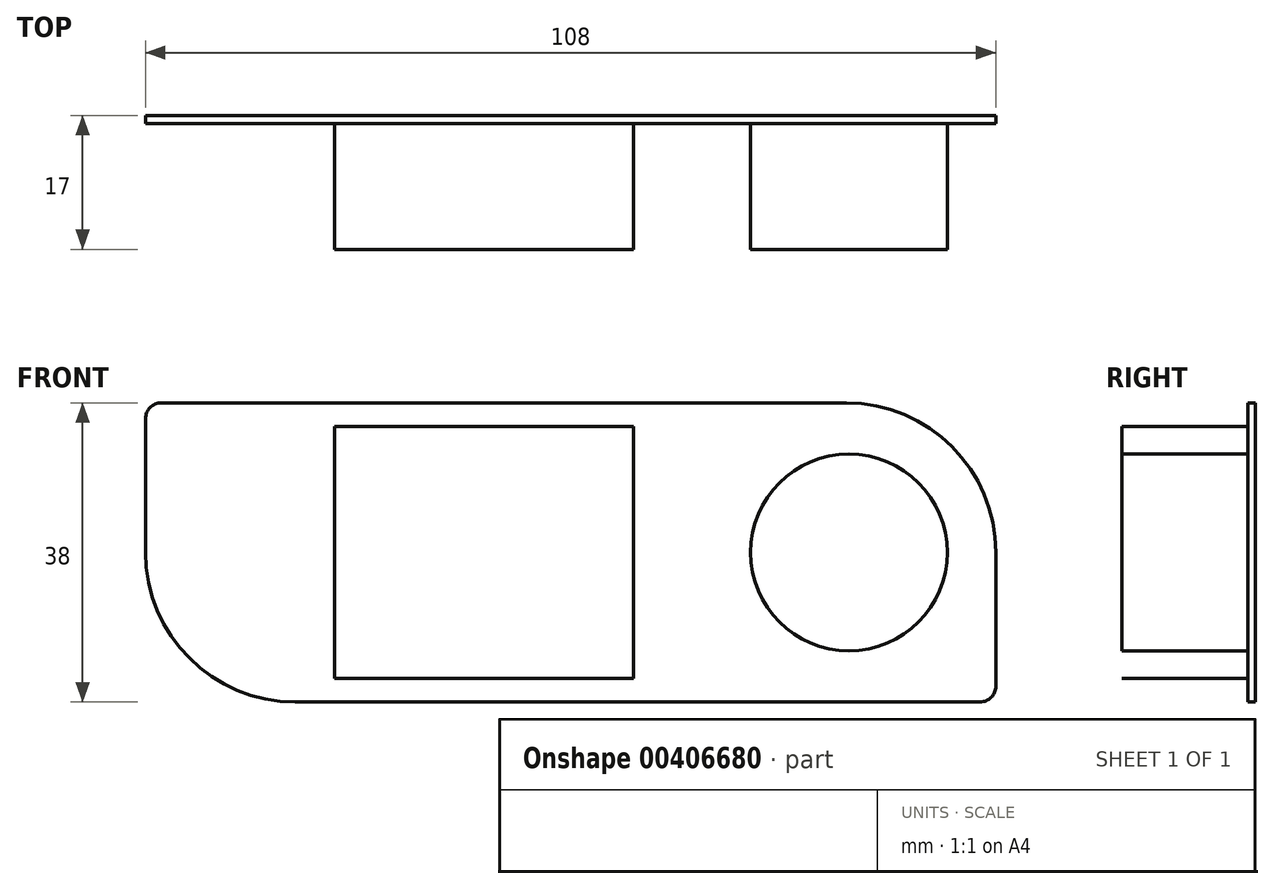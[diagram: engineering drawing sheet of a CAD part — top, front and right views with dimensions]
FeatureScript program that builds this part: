
annotation { "Feature Type Name" : "Feature", "Feature Type Description" : "" }
export const myFeature = defineFeature(function(context is Context, id is Id, definition is map)
    precondition{}
    {
        {
            var Q0;
            Q0=qCreatedBy(makeId("Front.planeOp"),FACE);
            var sketch = newSketch(context, id + "F0", { "sketchPlane" : qUnion([Q0])});
            skLineSegment(sketch, "E0.bottom", {"start": v(35, 19) * mm, "end": v(-52, 19) * mm});
            skLineSegment(sketch, "E0.top", {"start": v(52, -19) * mm, "end": v(-35, -19) * mm});
            skLineSegment(sketch, "E0.left", {"start": v(54, 0) * mm, "end": v(54, -17) * mm});
            skLineSegment(sketch, "E0.right", {"start": v(-54, 17) * mm, "end": v(-54, 0) * mm});
            skPoint(sketch, "E0.middle", {"position": v(0, 0) * mm});
            skPoint(sketch, "E1.visualSharp", {"position": v(-54, 19) * mm});
            skArc(sketch, "E1.filletArc", {"start": v(-52, 19) * mm, "mid": v(-53.41, 18.41) * mm, "end": v(-54, 17) * mm});
            skPoint(sketch, "E2.visualSharp", {"position": v(-54, -19) * mm});
            skArc(sketch, "E2.filletArc", {"start": v(-54, 0) * mm, "mid": v(-48.44, -13.44) * mm, "end": v(-35, -19) * mm});
            skPoint(sketch, "E3.visualSharp", {"position": v(54, 19) * mm});
            skArc(sketch, "E3.filletArc", {"start": v(54, 0) * mm, "mid": v(48.44, 13.44) * mm, "end": v(35, 19) * mm});
            skPoint(sketch, "E4.visualSharp", {"position": v(54, -19) * mm});
            skArc(sketch, "E4.filletArc", {"start": v(52, -19) * mm, "mid": v(53.41, -18.41) * mm, "end": v(54, -17) * mm});
            skSolve(sketch);
        }
        {
            var Q0;
            Q0=makeQuery(id+"F0.imprint","IMPRINT",FACE,{"disambiguationData":[TD([[makeQuery(id+"F0.imprint","IMPRINT",EDGE,{"derivedFrom":sQuery(id+"F0.wireOp",EDGE,"E0.bottom")}),1.0]])]});
            extrude(context, id + "F1", {"entities" : qUnion([Q0]), "depth" : 1 * mm});
        }
        {
            var Q0;
            Q0=makeQuery(id+"F1.opExtrude","CAP_FACE",FACE,{"disambiguationData":[OSD([sQuery(id+"F0.wireOp",EDGE,"E0.bottom"),sQuery(id+"F0.wireOp",EDGE,"E0.top"),sQuery(id+"F0.wireOp",EDGE,"E0.left"),sQuery(id+"F0.wireOp",EDGE,"E0.right"),sQuery(id+"F0.wireOp",EDGE,"E1.filletArc"),sQuery(id+"F0.wireOp",EDGE,"E2.filletArc"),sQuery(id+"F0.wireOp",EDGE,"E3.filletArc"),sQuery(id+"F0.wireOp",EDGE,"E4.filletArc")])],"isStart":false});
            var sketch = newSketch(context, id + "F2", { "sketchPlane" : qUnion([Q0])});
            skLineSegment(sketch, "E5.bottom", {"start": v(-30, 16) * mm, "end": v(8, 16) * mm});
            skLineSegment(sketch, "E5.top", {"start": v(-30, -16) * mm, "end": v(8, -16) * mm});
            skLineSegment(sketch, "E5.left", {"start": v(-30, 16) * mm, "end": v(-30, -16) * mm});
            skLineSegment(sketch, "E5.right", {"start": v(8, 16) * mm, "end": v(8, -16) * mm});
            skCircle(sketch, "E6", {"center": v(35.34, 0) * mm, "radius": 12.5 * mm});
            skLineSegment(sketch, "E7", {"start": v(0, 0) * mm, "end": v(-13.13, 0) * mm, "construction": true});
            skSolve(sketch);
        }
        {
            var Q0;
            Q0=makeQuery(id+"F2.imprint","IMPRINT",FACE,{"disambiguationData":[TD([[makeQuery(id+"F2.imprint","IMPRINT",EDGE,{"derivedFrom":sQuery(id+"F2.wireOp",EDGE,"E5.bottom")}),-1.0]])]});
            var Q1;
            Q1=makeQuery(id+"F2.imprint","IMPRINT",FACE,{"disambiguationData":[TD([[makeQuery(id+"F2.imprint","IMPRINT",EDGE,{"derivedFrom":sQuery(id+"F2.wireOp",EDGE,"E6")}),1.0]])]});
            extrude(context, id + "F3", {"entities" : qUnion([Q0, Q1]), "operationType" : NewBodyOperationType.ADD, "depth" : 16 * mm});
        }
    });
